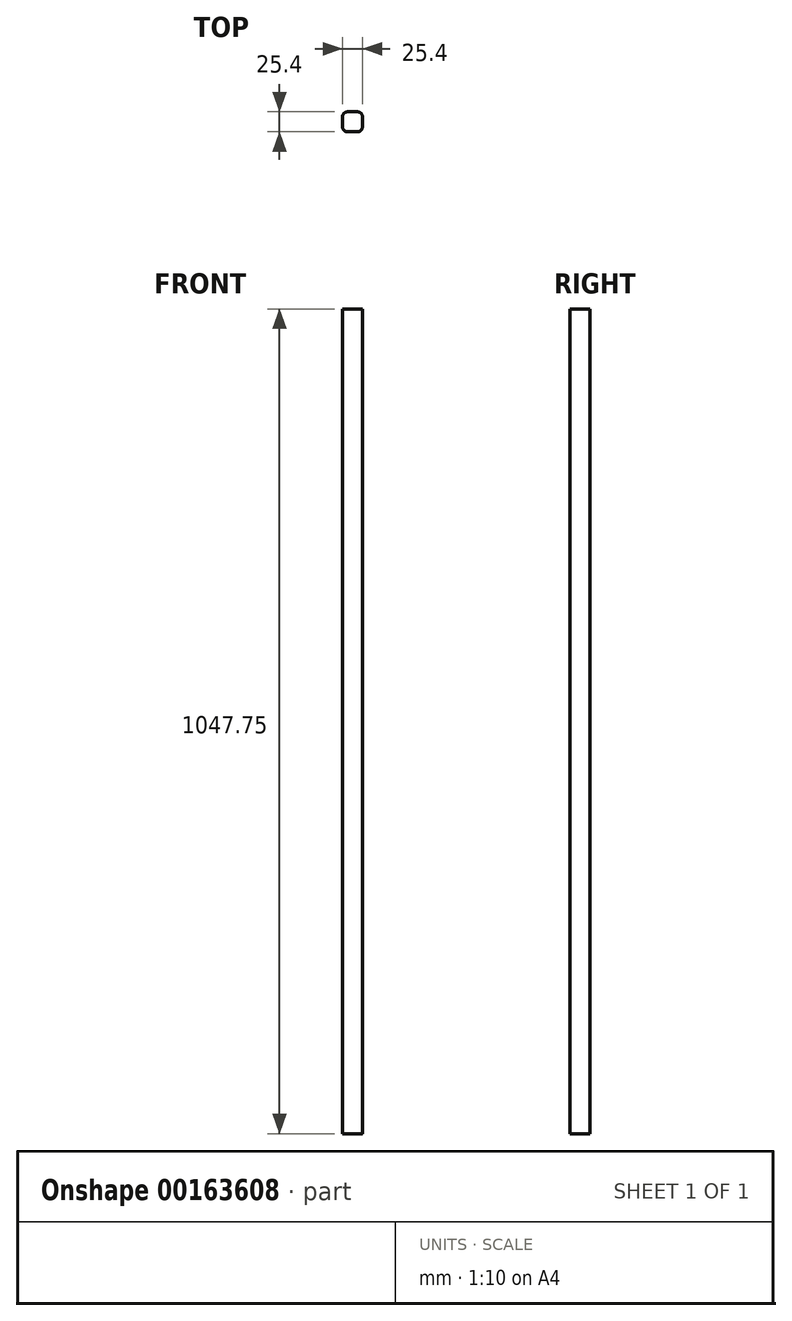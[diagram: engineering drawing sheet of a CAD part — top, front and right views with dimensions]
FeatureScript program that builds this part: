
annotation { "Feature Type Name" : "Feature", "Feature Type Description" : "" }
export const myFeature = defineFeature(function(context is Context, id is Id, definition is map)
    precondition{}
    {
        {
            var Q0;
            Q0=qCreatedBy(makeId("Top.planeOp"),FACE);
            var sketch = newSketch(context, id + "F0", { "sketchPlane" : qUnion([Q0])});
            skLineSegment(sketch, "E0.bottom", {"start": v(6.35, 12.7) * mm, "end": v(-6.35, 12.7) * mm});
            skLineSegment(sketch, "E0.top", {"start": v(6.35, -12.7) * mm, "end": v(-6.35, -12.7) * mm});
            skLineSegment(sketch, "E0.left", {"start": v(12.7, 6.35) * mm, "end": v(12.7, -6.35) * mm});
            skLineSegment(sketch, "E0.right", {"start": v(-12.7, 6.35) * mm, "end": v(-12.7, -6.35) * mm});
            skPoint(sketch, "E0.middle", {"position": v(0, 0) * mm});
            skPoint(sketch, "E1.visualSharp", {"position": v(-12.7, 12.7) * mm});
            skArc(sketch, "E1.filletArc", {"start": v(-6.35, 12.7) * mm, "mid": v(-10.84, 10.84) * mm, "end": v(-12.7, 6.35) * mm});
            skPoint(sketch, "E2.visualSharp", {"position": v(12.7, 12.7) * mm});
            skArc(sketch, "E2.filletArc", {"start": v(12.7, 6.35) * mm, "mid": v(10.84, 10.84) * mm, "end": v(6.35, 12.7) * mm});
            skPoint(sketch, "E3.visualSharp", {"position": v(12.7, -12.7) * mm});
            skArc(sketch, "E3.filletArc", {"start": v(6.35, -12.7) * mm, "mid": v(10.84, -10.84) * mm, "end": v(12.7, -6.35) * mm});
            skPoint(sketch, "E4.visualSharp", {"position": v(-12.7, -12.7) * mm});
            skArc(sketch, "E4.filletArc", {"start": v(-12.7, -6.35) * mm, "mid": v(-10.84, -10.84) * mm, "end": v(-6.35, -12.7) * mm});
            skSolve(sketch);
        }
        {
            var Q0;
            Q0=qSketchRegion(id+"F0",true);
            extrude(context, id + "F1", {"entities" : qUnion([Q0]), "depth" : 1047.75 * mm, "offsetDistance" : 25.4 * mm});
        }
    });
